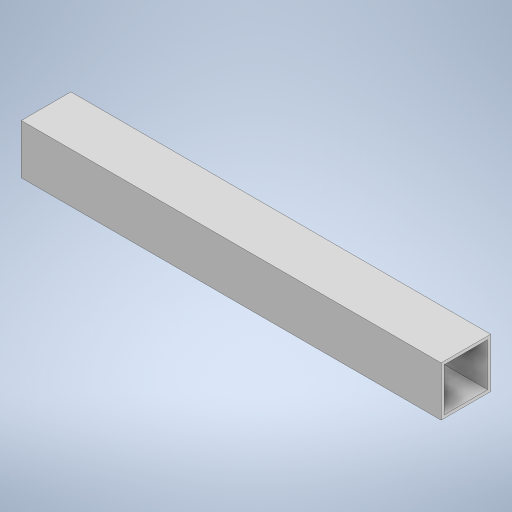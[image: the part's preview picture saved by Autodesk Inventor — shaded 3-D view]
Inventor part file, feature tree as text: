
AUTODESK INVENTOR PART (.ipt)
format: ipt  version: 2024 (Build 280153000, 153)  size: 220,160 bytes
history: native  units: in
note: dims shown in document units (in); Inventor stores cm internally (conversion verified against a paired STEP export)
features: extrude x1, sketch x1
ambient origin geometry x8: Origin, YZ Plane, XZ Plane, XY Plane, X Axis, Y Axis, Z Axis, Center Point
bodies: Solid1 (feature_tree)
feature tree (2):
  extrude  "Extrusion1"  Depth=1.0in
  sketch  "Sketch1"  dims[d0=1.0in d1=1.0in d2=0.0625in d3=8.465in d4=0.0in d5=0.5in d6=0.0344in d7=0.5in d8=0.0344in]
